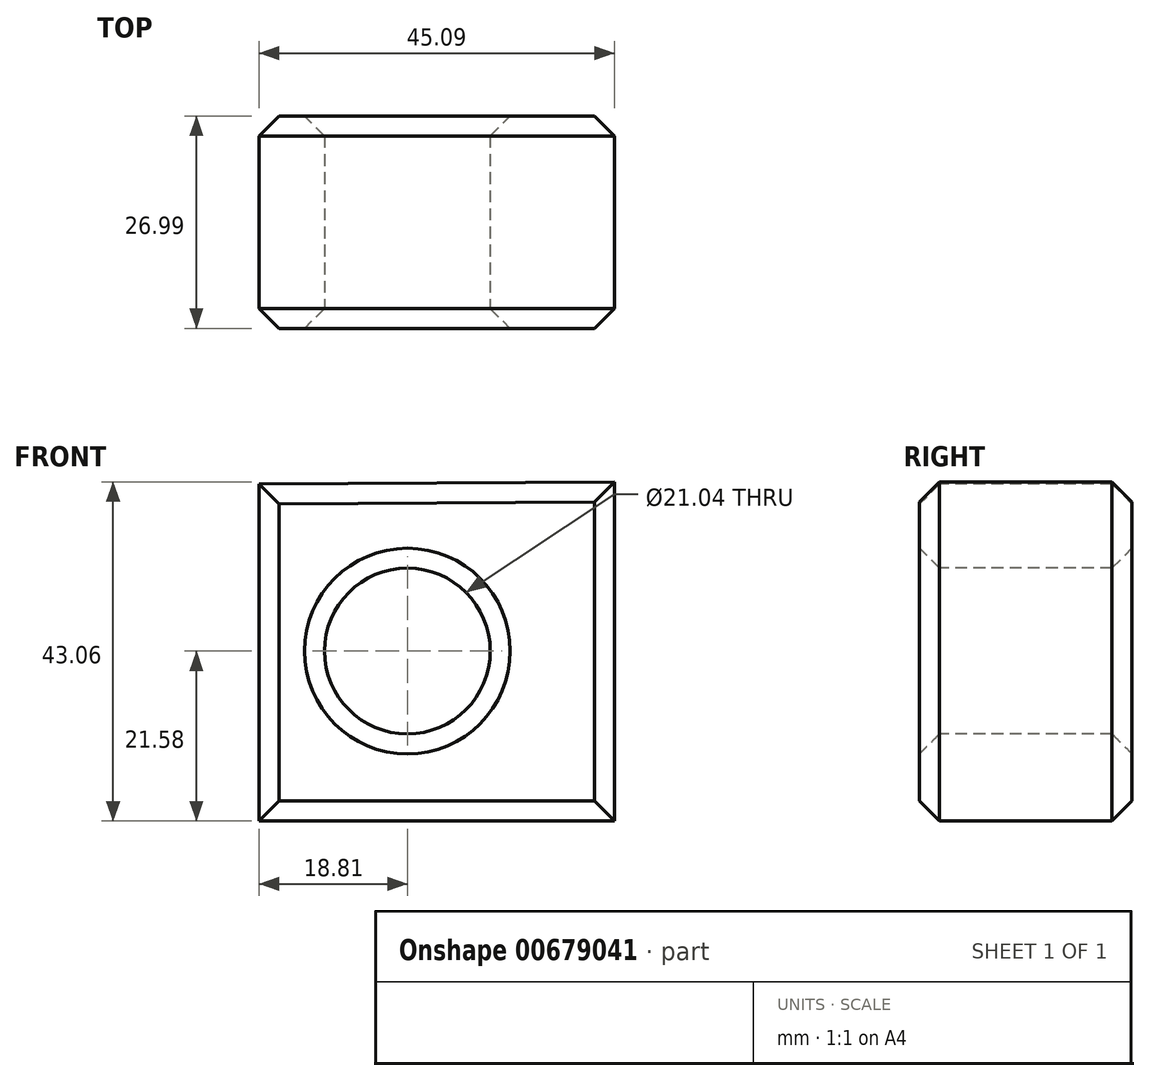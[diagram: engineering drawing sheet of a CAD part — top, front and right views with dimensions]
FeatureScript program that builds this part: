
annotation { "Feature Type Name" : "Feature", "Feature Type Description" : "" }
export const myFeature = defineFeature(function(context is Context, id is Id, definition is map)
    precondition{}
    {
        {
            var Q0;
            Q0=qCreatedBy(makeId("Front.planeOp"),FACE);
            var sketch = newSketch(context, id + "F0", { "sketchPlane" : qUnion([Q0])});
            skLineSegment(sketch, "E0", {"start": v(26.28, 21.48) * mm, "end": v(26.28, -21.58) * mm});
            skLineSegment(sketch, "E1", {"start": v(26.28, -21.58) * mm, "end": v(-18.81, -21.58) * mm});
            skLineSegment(sketch, "E2", {"start": v(-18.81, -21.58) * mm, "end": v(-18.81, 21.22) * mm});
            skLineSegment(sketch, "E3", {"start": v(-18.81, 21.22) * mm, "end": v(26.28, 21.48) * mm});
            skSolve(sketch);
        }
        {
            var Q0;
            Q0=makeQuery(id+"F0.imprint","IMPRINT",FACE,{"disambiguationData":[TD([[makeQuery(id+"F0.imprint","IMPRINT",EDGE,{"derivedFrom":sQuery(id+"F0.wireOp",EDGE,"E0")}),-1.0]])]});
            extrude(context, id + "F1", {"entities" : qUnion([Q0]), "oppositeDirection" : true, "depth" : 26.99 * mm, "offsetDistance" : 25.4 * mm});
        }
        {
            var Q0;
            Q0=makeQuery(id+"F1.opExtrude","CAP_FACE",FACE,{"disambiguationData":[OSD([sQuery(id+"F0.wireOp",EDGE,"E0"),sQuery(id+"F0.wireOp",EDGE,"E1"),sQuery(id+"F0.wireOp",EDGE,"E2"),sQuery(id+"F0.wireOp",EDGE,"E3")])],"isStart":true});
            var sketch = newSketch(context, id + "F2", { "sketchPlane" : qUnion([Q0])});
            skCircle(sketch, "E4", {"center": v(0, 0) * mm, "radius": 10.52 * mm});
            skSolve(sketch);
        }
        {
            var Q0;
            Q0=makeQuery(id+"F2.imprint","IMPRINT",FACE,{"disambiguationData":[TD([[makeQuery(id+"F2.imprint","IMPRINT",EDGE,{"derivedFrom":sQuery(id+"F2.wireOp",EDGE,"E4")}),1.0]])]});
            extrude(context, id + "F3", {"entities" : qUnion([Q0]), "operationType" : NewBodyOperationType.REMOVE, "endBound" : BoundingType.THROUGH_ALL, "oppositeDirection" : true, "depth" : 60.57 * mm, "offsetDistance" : 25.4 * mm});
        }
        {
            var Q0;
            Q0=makeQuery(id+"F1.opExtrude","CAP_FACE",FACE,{"disambiguationData":[OSD([sQuery(id+"F0.wireOp",EDGE,"E0"),sQuery(id+"F0.wireOp",EDGE,"E1"),sQuery(id+"F0.wireOp",EDGE,"E2"),sQuery(id+"F0.wireOp",EDGE,"E3")])],"isStart":false});
            chamfer(context, id + "F4", {"entities" : qUnion([Q0]), "width" : 2.54 * mm, "tangentPropagation" : true});
        }
        {
            var Q0;
            Q0=makeQuery(id+"F1.opExtrude","CAP_FACE",FACE,{"disambiguationData":[OSD([sQuery(id+"F0.wireOp",EDGE,"E0"),sQuery(id+"F0.wireOp",EDGE,"E1"),sQuery(id+"F0.wireOp",EDGE,"E2"),sQuery(id+"F0.wireOp",EDGE,"E3")])],"isStart":true});
            chamfer(context, id + "F5", {"entities" : qUnion([Q0]), "width" : 2.54 * mm, "tangentPropagation" : true});
        }
    });
